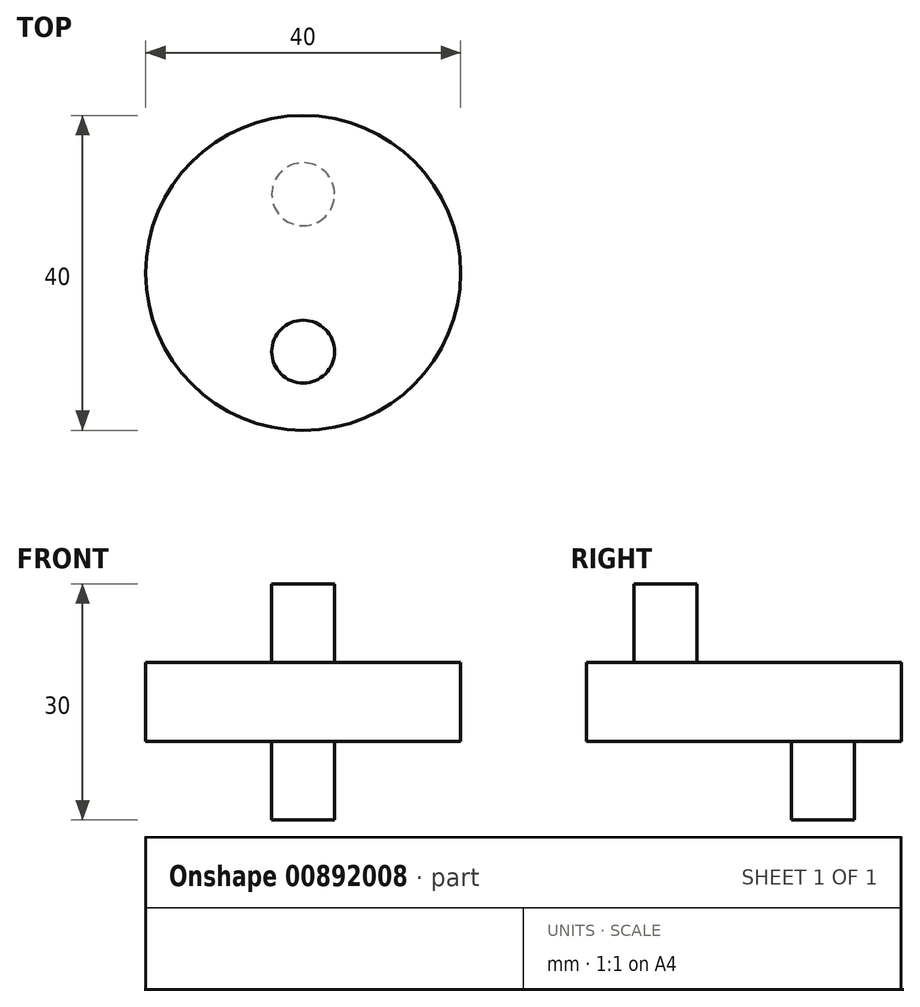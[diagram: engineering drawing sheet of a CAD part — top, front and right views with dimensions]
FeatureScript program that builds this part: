
annotation { "Feature Type Name" : "Feature", "Feature Type Description" : "" }
export const myFeature = defineFeature(function(context is Context, id is Id, definition is map)
    precondition{}
    {
        {
            var Q0;
            Q0=qCreatedBy(makeId("Top.planeOp"),FACE);
            var sketch = newSketch(context, id + "F0", { "sketchPlane" : qUnion([Q0])});
            skCircle(sketch, "E0", {"center": v(-38.42, 0) * mm, "radius": 20 * mm});
            skSolve(sketch);
        }
        {
            var Q0;
            Q0 = qSketchRegion(id + "F0", true);
            extrude(context, id + "F1", {"entities" : qUnion([Q0]), "depth" : 10 * mm, "offsetDistance" : 25 * mm});
        }
        {
            var Q0;
            Q0=makeQuery(id+"F1.opExtrude","CAP_FACE",FACE,{"disambiguationData":[OSD([sQuery(id+"F0.wireOp",EDGE,"E0")])],"isStart":false});
            var sketch = newSketch(context, id + "F2", { "sketchPlane" : qUnion([Q0])});
            skLineSegment(sketch, "E1", {"start": v(-38.42, 20) * mm, "end": v(-38.42, -20) * mm, "construction": true});
            skLineSegment(sketch, "E2", {"start": v(-58.42, 0) * mm, "end": v(-18.42, 0) * mm, "construction": true});
            skLineSegment(sketch, "E3", {"start": v(-55.74, 10) * mm, "end": v(-21.1, 10) * mm, "construction": true});
            skLineSegment(sketch, "E4", {"start": v(-55.74, -10) * mm, "end": v(-21.1, -10) * mm, "construction": true});
            skCircle(sketch, "E5", {"center": v(-38.42, -10) * mm, "radius": 4 * mm});
            skSolve(sketch);
        }
        {
            var Q0;
            Q0 = qSketchRegion(id + "F2", true);
            extrude(context, id + "F3", {"entities" : qUnion([Q0]), "operationType" : NewBodyOperationType.ADD, "depth" : 10 * mm, "offsetDistance" : 25 * mm});
        }
        {
            var Q0;
            Q0=makeQuery(id+"F1.opExtrude","CAP_FACE",FACE,{"disambiguationData":[OSD([sQuery(id+"F0.wireOp",EDGE,"E0")])],"isStart":true});
            var sketch = newSketch(context, id + "F4", { "sketchPlane" : qUnion([Q0])});
            skLineSegment(sketch, "E6", {"start": v(-58.42, 0) * mm, "end": v(-18.42, 0) * mm, "construction": true});
            skLineSegment(sketch, "E7", {"start": v(-38.42, 20) * mm, "end": v(-38.42, -20) * mm, "construction": true});
            skLineSegment(sketch, "E8", {"start": v(-55.74, 10) * mm, "end": v(-21.1, 10) * mm, "construction": true});
            skLineSegment(sketch, "E9", {"start": v(-55.74, -10) * mm, "end": v(-21.1, -10) * mm, "construction": true});
            skCircle(sketch, "E10", {"center": v(-38.42, -10) * mm, "radius": 4 * mm});
            skSolve(sketch);
        }
        {
            var Q0;
            Q0 = qSketchRegion(id + "F4", true);
            extrude(context, id + "F5", {"entities" : qUnion([Q0]), "operationType" : NewBodyOperationType.ADD, "depth" : 10 * mm, "offsetDistance" : 25 * mm});
        }
    });
